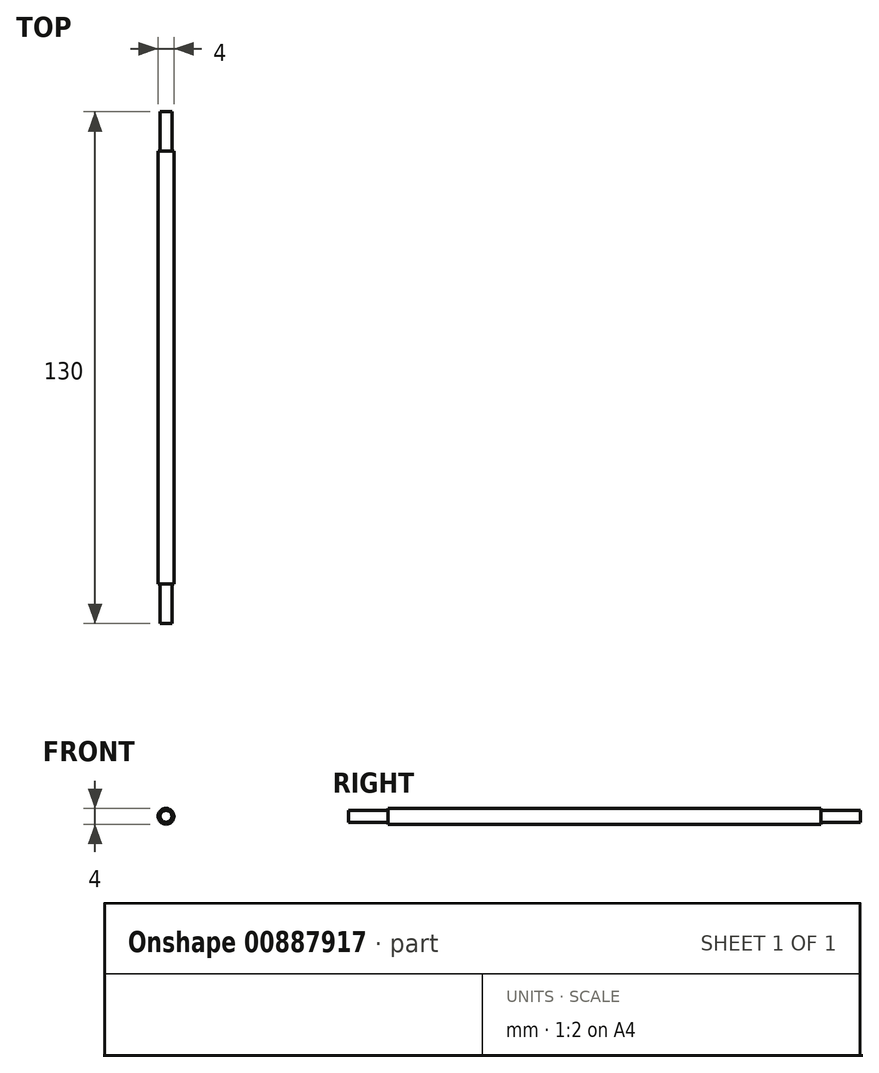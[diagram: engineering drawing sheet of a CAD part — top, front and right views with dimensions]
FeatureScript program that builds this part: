
annotation { "Feature Type Name" : "Feature", "Feature Type Description" : "" }
export const myFeature = defineFeature(function(context is Context, id is Id, definition is map)
    precondition{}
    {
        {
            var Q0;
            Q0=qCreatedBy(makeId("Front.planeOp"),FACE);
            var sketch = newSketch(context, id + "F0", { "sketchPlane" : qUnion([Q0])});
            skCircle(sketch, "E0", {"center": v(0, 0) * mm, "radius": 2 * mm});
            skSolve(sketch);
        }
        {
            var Q0;
            Q0 = qSketchRegion(id + "F0", true);
            extrude(context, id + "F1", {"entities" : qUnion([Q0]), "endBound" : BoundingType.SYMMETRIC, "depth" : 130 * mm, "offsetDistance" : 25 * mm});
        }
        {
            var Q0;
            Q0=makeQuery(id+"F1.opExtrude","CAP_FACE",FACE,{"disambiguationData":[OSD([sQuery(id+"F0.wireOp",EDGE,"E0")])],"isStart":false});
            var sketch = newSketch(context, id + "F2", { "sketchPlane" : qUnion([Q0])});
            skCircle(sketch, "E1", {"center": v(0, 0) * mm, "radius": 1.5 * mm});
            skSolve(sketch);
        }
        {
            var Q0;
            Q0=makeQuery(id+"F2.imprint","IMPRINT",FACE,{"disambiguationData":[TD([[makeQuery(id+"F2.imprint","IMPRINT",EDGE,{"derivedFrom":sQuery(id+"F2.wireOp",EDGE,"E1")}),-1.0]])]});
            var Q1;
            Q1=sQuery(id+"F2.wireOp",EDGE,"E1");
            extrude(context, id + "F3", {"entities" : qUnion([Q0]), "operationType" : NewBodyOperationType.REMOVE, "surfaceOperationType" : NewSurfaceOperationType.ADD, "surfaceEntities" : qUnion([Q1]), "oppositeDirection" : true, "depth" : 10 * mm, "offsetDistance" : 25 * mm});
        }
        {
            var Q0;
            Q0=makeQuery(id+"F1.opExtrude","CAP_FACE",FACE,{"disambiguationData":[OSD([sQuery(id+"F0.wireOp",EDGE,"E0")])],"isStart":true});
            var sketch = newSketch(context, id + "F4", { "sketchPlane" : qUnion([Q0])});
            skCircle(sketch, "E2", {"center": v(0, 0) * mm, "radius": 1.5 * mm});
            skSolve(sketch);
        }
        {
            var Q0;
            Q0=makeQuery(id+"F4.imprint","IMPRINT",FACE,{"disambiguationData":[TD([[makeQuery(id+"F4.imprint","IMPRINT",EDGE,{"derivedFrom":sQuery(id+"F4.wireOp",EDGE,"E2")}),-1.0]])]});
            extrude(context, id + "F5", {"entities" : qUnion([Q0]), "operationType" : NewBodyOperationType.REMOVE, "oppositeDirection" : true, "depth" : 10 * mm, "offsetDistance" : 25 * mm});
        }
    });
